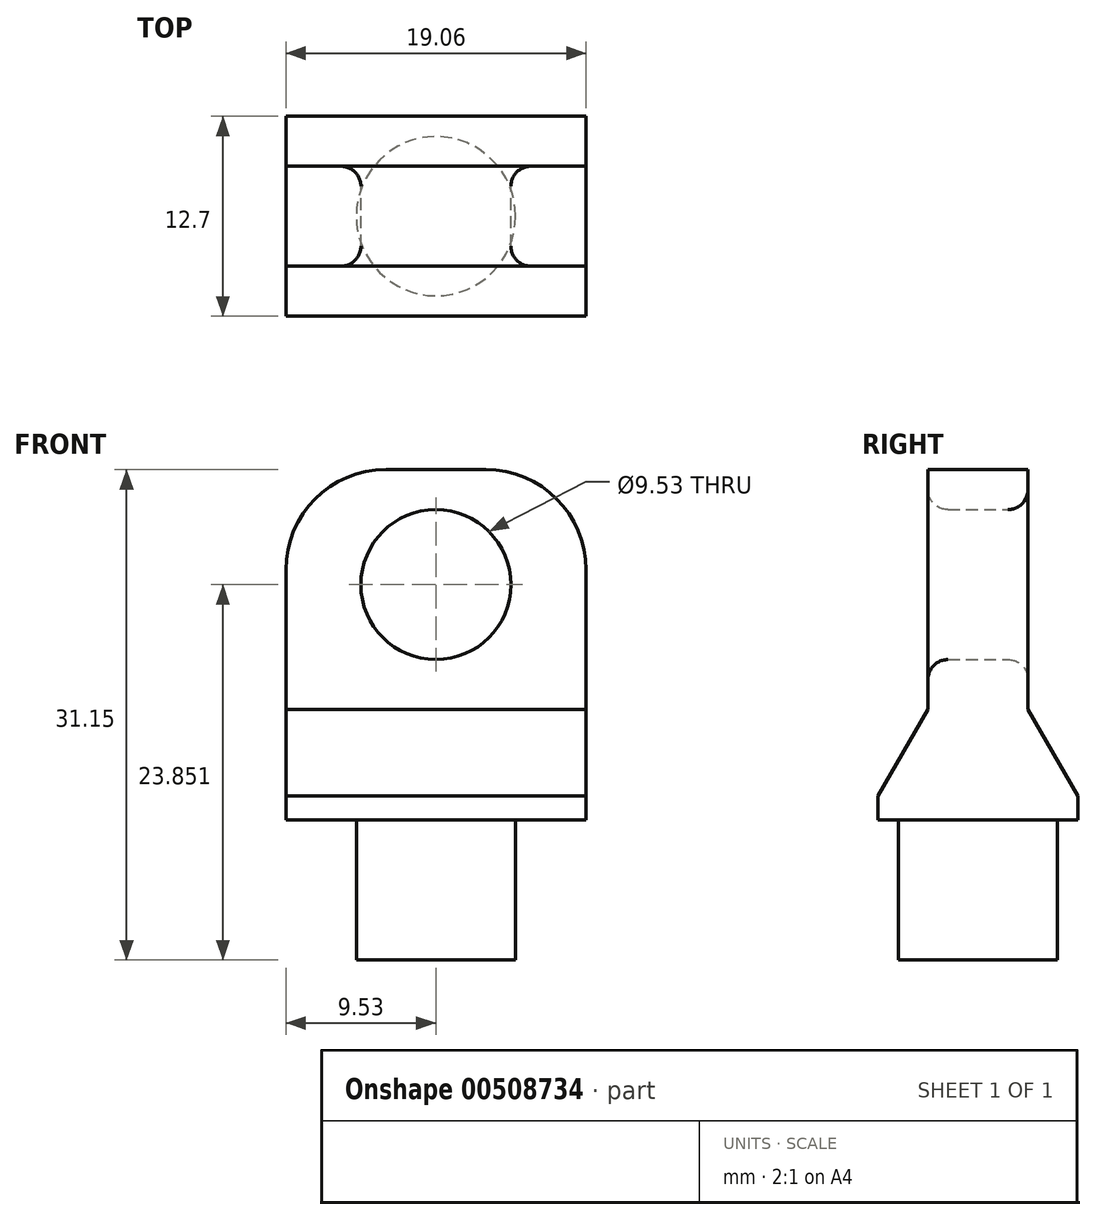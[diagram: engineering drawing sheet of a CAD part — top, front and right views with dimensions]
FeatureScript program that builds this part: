
annotation { "Feature Type Name" : "Feature", "Feature Type Description" : "" }
export const myFeature = defineFeature(function(context is Context, id is Id, definition is map)
    precondition{}
    {
        {
            var Q0;
            Q0=qCreatedBy(makeId("Front.planeOp"),FACE);
            var sketch = newSketch(context, id + "F0", { "sketchPlane" : qUnion([Q0])});
            skLineSegment(sketch, "E0", {"start": v(0, 0) * mm, "end": v(5.05, 0) * mm});
            skLineSegment(sketch, "E1", {"start": v(5.05, 0) * mm, "end": v(5.05, -8.9) * mm});
            skLineSegment(sketch, "E2", {"start": v(5.05, -8.9) * mm, "end": v(0, -8.9) * mm});
            skLineSegment(sketch, "E3", {"start": v(0, -8.9) * mm, "end": v(0, 0) * mm});
            skSolve(sketch);
        }
        {
            var Q0;
            Q0=makeQuery(id+"F0.imprint","IMPRINT",FACE,{"disambiguationData":[TD([[makeQuery(id+"F0.imprint","IMPRINT",EDGE,{"derivedFrom":sQuery(id+"F0.wireOp",EDGE,"E0")}),-1.0]])]});
            var Q1;
            Q1=sQuery(id+"F0.wireOp",EDGE,"E3");
            revolve(context, id + "F1", {"entities" : qUnion([Q0]), "axis" : qUnion([Q1]), "revolveType" : RevolveType.FULL});
        }
        {
            var Q0;
            Q0=qCreatedBy(makeId("Right.planeOp"),FACE);
            var sketch = newSketch(context, id + "F2", { "sketchPlane" : qUnion([Q0])});
            skLineSegment(sketch, "E4", {"start": v(-6.35, 0) * mm, "end": v(6.35, 0) * mm});
            skLineSegment(sketch, "E5", {"start": v(6.35, 0) * mm, "end": v(6.35, 1.52) * mm});
            skLineSegment(sketch, "E6", {"start": v(6.35, 1.52) * mm, "end": v(3.18, 7.02) * mm});
            skLineSegment(sketch, "E7", {"start": v(3.18, 7.02) * mm, "end": v(3.17, 22.26) * mm});
            skLineSegment(sketch, "E8", {"start": v(3.18, 22.26) * mm, "end": v(-3.18, 22.26) * mm});
            skLineSegment(sketch, "E9", {"start": v(-3.18, 22.26) * mm, "end": v(-3.17, 7.02) * mm});
            skLineSegment(sketch, "E10", {"start": v(-3.18, 7.02) * mm, "end": v(-6.35, 1.52) * mm});
            skLineSegment(sketch, "E11", {"start": v(-6.35, 1.52) * mm, "end": v(-6.35, 0) * mm});
            skSolve(sketch);
        }
        {
            var Q0;
            Q0=makeQuery(id+"F2.imprint","IMPRINT",FACE,{"disambiguationData":[TD([[makeQuery(id+"F2.imprint","IMPRINT",EDGE,{"derivedFrom":sQuery(id+"F2.wireOp",EDGE,"E4")}),1.0]])]});
            extrude(context, id + "F3", {"entities" : qUnion([Q0]), "operationType" : NewBodyOperationType.ADD, "endBound" : BoundingType.SYMMETRIC, "depth" : 19.05 * mm, "offsetDistance" : 25.4 * mm});
        }
        {
            var Q0;
            Q0=makeQuery(id+"F3.opExtrude","CAP_EDGE",EDGE,{"disambiguationData":[OSD([sQuery(id+"F2.wireOp",EDGE,"E8")])],"isStart":false});
            var Q1;
            Q1=makeQuery(id+"F3.opExtrude","CAP_EDGE",EDGE,{"disambiguationData":[OSD([sQuery(id+"F2.wireOp",EDGE,"E8")])],"isStart":true});
            fillet(context, id + "F4", {"entities" : qUnion([Q0, Q1]), "radius" : 6.35 * mm, "tangentPropagation" : true, "allowEdgeOverflow" : false});
        }
        {
            var Q0;
            Q0=qCreatedBy(makeId("Front.planeOp"),FACE);
            var sketch = newSketch(context, id + "F5", { "sketchPlane" : qUnion([Q0])});
            skCircle(sketch, "E12", {"center": v(0, 14.96) * mm, "radius": 4.76 * mm});
            skSolve(sketch);
        }
        {
            var Q0;
            Q0 = qSketchRegion(id + "F5", true);
            extrude(context, id + "F6", {"entities" : qUnion([Q0]), "operationType" : NewBodyOperationType.REMOVE, "endBound" : BoundingType.THROUGH_ALL, "depth" : 25.4 * mm, "offsetDistance" : 25.4 * mm, "hasSecondDirection" : true, "secondDirectionBound" : SecondDirectionBoundingType.THROUGH_ALL, "secondDirectionOppositeDirection" : true, "secondDirectionDepth" : 25.4 * mm});
        }
        {
            var Q0;
            Q0=makeQuery(id+"F6.boolean.opBoolean","INTERSECT",EDGE,{"derivedFrom":[makeQuery(id+"F3.opExtrude","SWEPT_FACE",FACE,{"disambiguationData":[OSD([sQuery(id+"F2.wireOp",EDGE,"E9")])]}),makeQuery(id+"F6.opExtrude","SWEPT_FACE",FACE,{"disambiguationData":[OSD([sQuery(id+"F5.wireOp",EDGE,"E12")])]})]});
            var Q1;
            Q1=makeQuery(id+"F6.boolean.opBoolean","INTERSECT",EDGE,{"derivedFrom":[makeQuery(id+"F3.opExtrude","SWEPT_FACE",FACE,{"disambiguationData":[OSD([sQuery(id+"F2.wireOp",EDGE,"E7")])]}),makeQuery(id+"F6.opExtrude","SWEPT_FACE",FACE,{"disambiguationData":[OSD([sQuery(id+"F5.wireOp",EDGE,"E12")])]})]});
            fillet(context, id + "F7", {"entities" : qUnion([Q0, Q1]), "radius" : 1.27 * mm, "tangentPropagation" : true, "allowEdgeOverflow" : false});
        }
    });
